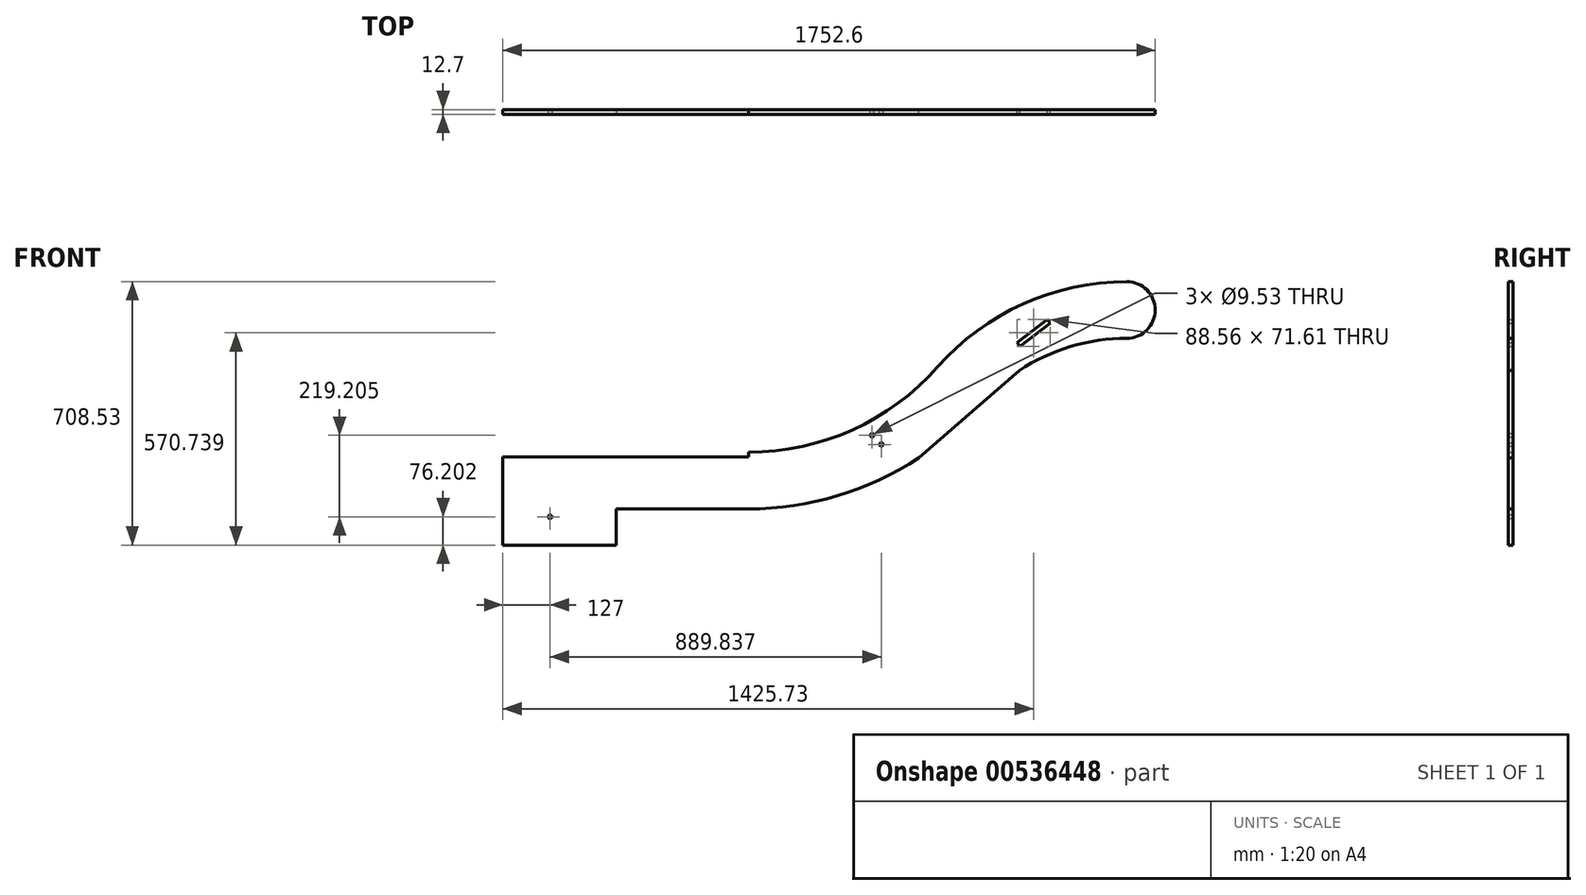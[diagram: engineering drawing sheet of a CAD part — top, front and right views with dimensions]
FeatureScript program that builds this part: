
annotation { "Feature Type Name" : "Feature", "Feature Type Description" : "" }
export const myFeature = defineFeature(function(context is Context, id is Id, definition is map)
    precondition{}
    {
        {
            var Q0;
            Q0=qCreatedBy(makeId("Front.planeOp"),FACE);
            var sketch = newSketch(context, id + "F0", { "sketchPlane" : qUnion([Q0])});
            skLineSegment(sketch, "E0", {"start": v(-1078.95, 584.06) * mm, "end": v(-570.95, 584.06) * mm, "construction": true});
            skLineSegment(sketch, "E1", {"start": v(-570.95, 584.06) * mm, "end": v(-570.95, 1042.7) * mm, "construction": true});
            skLineSegment(sketch, "E2", {"start": v(-570.95, 1042.7) * mm, "end": v(-62.95, 1042.7) * mm, "construction": true});
            skLineSegment(sketch, "E3", {"start": v(-1078.95, 57.8) * mm, "end": v(-1078.95, 584.06) * mm, "construction": true});
            skArc(sketch, "E4", {"start": v(-1078.95, 584.06) * mm, "mid": v(-800.27, 644.05) * mm, "end": v(-570.95, 813.38) * mm});
            skArc(sketch, "E5", {"start": v(-62.95, 1042.7) * mm, "mid": v(-341.63, 982.72) * mm, "end": v(-570.95, 813.38) * mm});
            skArc(sketch, "E6.0", {"start": v(-1078.95, 431.66) * mm, "mid": v(-840.53, 466.66) * mm, "end": v(-622.22, 568.68) * mm});
            skArc(sketch, "E7.0", {"start": v(-62.95, 890.3) * mm, "mid": v(-213.79, 868.16) * mm, "end": v(-351.9, 803.62) * mm});
            skLineSegment(sketch, "E8", {"start": v(-351.9, 803.62) * mm, "end": v(-622.22, 568.68) * mm});
            skLineSegment(sketch, "E9.bottom", {"start": v(-1078.95, 584.06) * mm, "end": v(-1078.95, 584.06) * mm});
            skLineSegment(sketch, "E9.top", {"start": v(-1078.95, 431.66) * mm, "end": v(-1739.35, 431.66) * mm});
            skLineSegment(sketch, "E9.left", {"start": v(-1078.95, 584.06) * mm, "end": v(-1078.95, 431.66) * mm, "construction": true});
            skLineSegment(sketch, "E9.right", {"start": v(-1739.35, 571.36) * mm, "end": v(-1739.35, 517.39) * mm});
            skArc(sketch, "E10", {"start": v(-62.95, 890.3) * mm, "mid": v(13.25, 966.5) * mm, "end": v(-62.95, 1042.7) * mm});
            skPoint(sketch, "E11.start.orphan", {"position": v(-1739.35, 507.86) * mm});
            skLineSegment(sketch, "E12.trimOffspring", {"start": v(-1739.35, 498.34) * mm, "end": v(-1739.35, 431.66) * mm});
            skArc(sketch, "E13.0", {"start": v(-62.95, 966.5) * mm, "mid": v(-193.3, 952.2) * mm, "end": v(-317.46, 909.96) * mm, "construction": true});
            skLineSegment(sketch, "E14", {"start": v(-317.46, 909.96) * mm, "end": v(-62.95, 365.37) * mm, "construction": true});
            skLineSegment(sketch, "E15", {"start": v(-62.95, 966.5) * mm, "end": v(-62.95, 365.37) * mm, "construction": true});
            skLineSegment(sketch, "E16", {"start": v(-62.95, 365.37) * mm, "end": v(-278.14, 1082.67) * mm, "construction": true});
            skPoint(sketch, "E17.start.orphan", {"position": v(-193.3, 952.2) * mm});
            skLineSegment(sketch, "E18", {"start": v(-774.15, 656.52) * mm, "end": v(-774.15, 437.24) * mm, "construction": true});
            skLineSegment(sketch, "E19", {"start": v(-774.15, 656.52) * mm, "end": v(-342.44, 224.8) * mm, "construction": true});
            skLineSegment(sketch, "E20", {"start": v(-774.15, 656.52) * mm, "end": v(-723.35, 707.31) * mm, "construction": true});
            skLineSegment(sketch, "E21.0", {"start": v(-747.2, 629.58) * mm, "end": v(-696.41, 680.37) * mm, "construction": true});
            skCircle(sketch, "E22", {"center": v(-747.2, 629.58) * mm, "radius": 4.76 * mm});
            skLineSegment(sketch, "E23.0", {"start": v(-722.51, 604.88) * mm, "end": v(-671.72, 655.68) * mm, "construction": true});
            skCircle(sketch, "E24", {"center": v(-722.51, 604.88) * mm, "radius": 4.76 * mm});
            skLineSegment(sketch, "E25", {"start": v(-1739.35, 517.39) * mm, "end": v(-1739.35, 498.34) * mm});
            skLineSegment(sketch, "E26.top", {"start": v(-1739.35, 571.36) * mm, "end": v(-1078.95, 571.36) * mm});
            skLineSegment(sketch, "E26.right", {"start": v(-1078.95, 584.06) * mm, "end": v(-1078.95, 571.36) * mm});
            skPoint(sketch, "E27.orphan", {"position": v(-1739.35, 584.06) * mm});
            skLineSegment(sketch, "E28.0", {"start": v(-350.21, 869.1) * mm, "end": v(-378.76, 847.39) * mm});
            skLineSegment(sketch, "E29.MirrorCS", {"start": v(-317.46, 909.96) * mm, "end": v(-277.03, 940.72) * mm});
            skLineSegment(sketch, "E30", {"start": v(-1739.35, 571.36) * mm, "end": v(-1739.35, 431.66) * mm});
            skLineSegment(sketch, "E31", {"start": v(-277.03, 940.72) * mm, "end": v(-269.34, 930.6) * mm});
            skLineSegment(sketch, "E32", {"start": v(-317.46, 909.96) * mm, "end": v(-357.9, 879.21) * mm});
            skLineSegment(sketch, "E33", {"start": v(-350.21, 869.1) * mm, "end": v(-357.9, 879.21) * mm});
            skLineSegment(sketch, "E34", {"start": v(-378.76, 847.39) * mm, "end": v(-269.34, 930.6) * mm});
            skLineSegment(sketch, "E35", {"start": v(-241.17, 948.18) * mm, "end": v(-233.48, 938.07) * mm});
            skLineSegment(sketch, "E36.1.0", {"start": v(-408.17, 857.5) * mm, "end": v(-62.95, 365.37) * mm, "construction": true});
            skLineSegment(sketch, "E36.anchor1", {"start": v(-62.95, 365.37) * mm, "end": v(-317.46, 909.96) * mm, "construction": true});
            skLineSegment(sketch, "E36.anchor2", {"start": v(-62.95, 365.37) * mm, "end": v(-488.38, 790.07) * mm, "construction": true});
            skLineSegment(sketch, "E37.0", {"start": v(-774.15, 584.06) * mm, "end": v(-774.15, 431.66) * mm, "construction": true});
            skLineSegment(sketch, "E38", {"start": v(-774.15, 584.06) * mm, "end": v(-774.15, 656.52) * mm, "construction": true});
            skSolve(sketch);
        }
        {
            var Q0;
            Q0 = qSketchRegion(id + "F0", true);
            extrude(context, id + "F1", {"entities" : qUnion([Q0]), "depth" : 12.7 * mm, "offsetDistance" : 25.4 * mm});
        }
        {
            var Q0;
            Q0=makeQuery(id+"F1.opExtrude","CAP_FACE",FACE,{"disambiguationData":[OSD([sQuery(id+"F0.wireOp",EDGE,"E4"),sQuery(id+"F0.wireOp",EDGE,"E5"),sQuery(id+"F0.wireOp",EDGE,"E6.0"),sQuery(id+"F0.wireOp",EDGE,"E7.0"),sQuery(id+"F0.wireOp",EDGE,"E8"),sQuery(id+"F0.wireOp",EDGE,"E9.bottom"),sQuery(id+"F0.wireOp",EDGE,"E9.top"),sQuery(id+"F0.wireOp",EDGE,"E10"),sQuery(id+"F0.wireOp",EDGE,"E22"),sQuery(id+"F0.wireOp",EDGE,"E24"),sQuery(id+"F0.wireOp",EDGE,"E26.top"),sQuery(id+"F0.wireOp",EDGE,"E26.right"),sQuery(id+"F0.wireOp",EDGE,"rGuNlkWs-DwgR-RLvr-mMdR-KLj3d7VYUrrU"),sQuery(id+"F0.wireOp",EDGE,"E28.0"),sQuery(id+"F0.wireOp",EDGE,"E29.MirrorCS"),sQuery(id+"F0.wireOp",EDGE,"bdf513aa-e08c-4932-959c-efffc82560380.MirrorCS"),sQuery(id+"F0.wireOp",EDGE,"18Rq9EtM-grnE-uFA9-u4ZY-gGSRGGMkSvjP"),sQuery(id+"F0.wireOp",EDGE,"AyWyaUEp-hzy5-DDg5-a3wd-rfjwWbH5fqIC"),sQuery(id+"F0.wireOp",EDGE,"E30")])],"isStart":false});
            var sketch = newSketch(context, id + "F2", { "sketchPlane" : qUnion([Q0])});
            skLineSegment(sketch, "E39", {"start": v(-317.46, 909.96) * mm, "end": v(-9.94, 505.62) * mm, "construction": true});
            skCircle(sketch, "E40", {"center": v(-9.94, 505.62) * mm, "radius": 254 * mm, "construction": true});
            skLineSegment(sketch, "E41", {"start": v(-9.94, 251.62) * mm, "end": v(-1739.35, 251.62) * mm, "construction": true});
            skLineSegment(sketch, "E42.top", {"start": v(-1739.35, 431.66) * mm, "end": v(-1741.67, 431.66) * mm});
            skLineSegment(sketch, "E43", {"start": v(-1739.35, 251.62) * mm, "end": v(-1739.35, 431.66) * mm});
            skLineSegment(sketch, "E44.0", {"start": v(-1612.35, -106.65) * mm, "end": v(-1612.35, 431.66) * mm, "construction": true});
            skCircle(sketch, "E45", {"center": v(-1612.35, 410.37) * mm, "radius": 4.76 * mm});
            skLineSegment(sketch, "E46.left", {"start": v(-1739.35, 45.75) * mm, "end": v(-1739.35, -30.45) * mm});
            skLineSegment(sketch, "E47.0", {"start": v(-1434.55, 334.17) * mm, "end": v(-1434.55, 431.66) * mm});
            skLineSegment(sketch, "E48.trimOffspring", {"start": v(-1434.55, 334.17) * mm, "end": v(-1739.35, 334.17) * mm});
            skLineSegment(sketch, "E49.trimOffspring", {"start": v(-1434.55, 410.37) * mm, "end": v(-1603.53, 410.37) * mm, "construction": true});
            skLineSegment(sketch, "E50", {"start": v(-1739.35, 431.66) * mm, "end": v(-1434.55, 431.66) * mm});
            skSolve(sketch);
        }
        {
            var Q0;
            Q0 = qSketchRegion(id + "F2", true);
            extrude(context, id + "F3", {"entities" : qUnion([Q0]), "operationType" : NewBodyOperationType.ADD, "oppositeDirection" : true, "depth" : 12.7 * mm, "offsetDistance" : 25.4 * mm});
        }
    });
